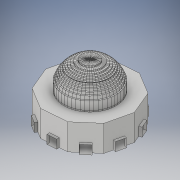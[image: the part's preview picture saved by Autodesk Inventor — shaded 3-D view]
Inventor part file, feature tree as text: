
AUTODESK INVENTOR PART (.ipt)
format: ipt  version: 2017 (Build 210142000, 142)  size: 1,995,776 bytes
history: native  units: in
note: dims shown in document units (in); Inventor stores cm internally (conversion verified against a paired STEP export)
features: extrude x8, sketch x7, other x3, pattern_circular x2, plane x1
ambient origin geometry x8: Origin, YZ Plane, XZ Plane, XY Plane, X Axis, Y Axis, Z Axis, Center Point
bodies: Solid1 (feature_tree)
feature tree (21):
  extrude  "bace"  Depth=1.0in TaperAngle=0.0deg
  extrude  "bace wall"  Depth=1.0in TaperAngle=0.0deg
  extrude  "bace ceiling"  Depth=1.0in
  other  "used to find the workplane for the dome"
  plane  "workplane for dome"
  extrude  "dome make"  Depth=1.0in TaperAngle=0.0deg
  sketch  "Sketch18"  dims[d190=45.0deg d192=1.0in d193=1.0in d194=1.0in d195=1.0in d196=1.0in d197=1.0in d198=1.0in d199=1.0in d200=0.0in d201=1.0in d202=0.0in d204=1.0in d205=19.685in d206=360.0deg d208=1.0in d209=3.937in d210=360.0deg]
  extrude  "dome part cut 1"  Depth=2.5166in TaperAngle=90.0deg
  extrude  "dome part cut 2"  Depth=42.0in
  pattern_circular  "Circular Pattern6"  [2 undecoded]
  extrude  "door frame"  Depth=1.0in
  extrude  "corridor connection"  Depth=1.0in
  pattern_circular  "Circular Pattern of corridor connection"  [2 undecoded]
  other  "Delete Faces of the room"
  other  "Delete Faces of dome"
  sketch  "Sketch1"  dims[d0=62.0in d1=1.0in d2=0.0in]
  sketch  "Sketch2"  dims[d4=1.0in d5=20.0in d6=0.0in]
  sketch  "Sketch3"  dims[d8=1.0in d9=0.0in d16=3.5in d17=6.6667in]
  sketch  "Sketch8"  dims[d18=1.0in d19=0.0in d107=1.0in d108=0.0in]
  sketch  "Sketch12"  dims[d109=40.0in d110=90.0deg d166=2.5166in]
  sketch  "Sketch17"  dims[d186=21.0in d187=0.0in d189=42.0in]
note: 4 required parameter values undecoded (feature->parameter linkage not recoverable at this tier; creation-order binding heuristic only, values carry confidence <= 0.55)
